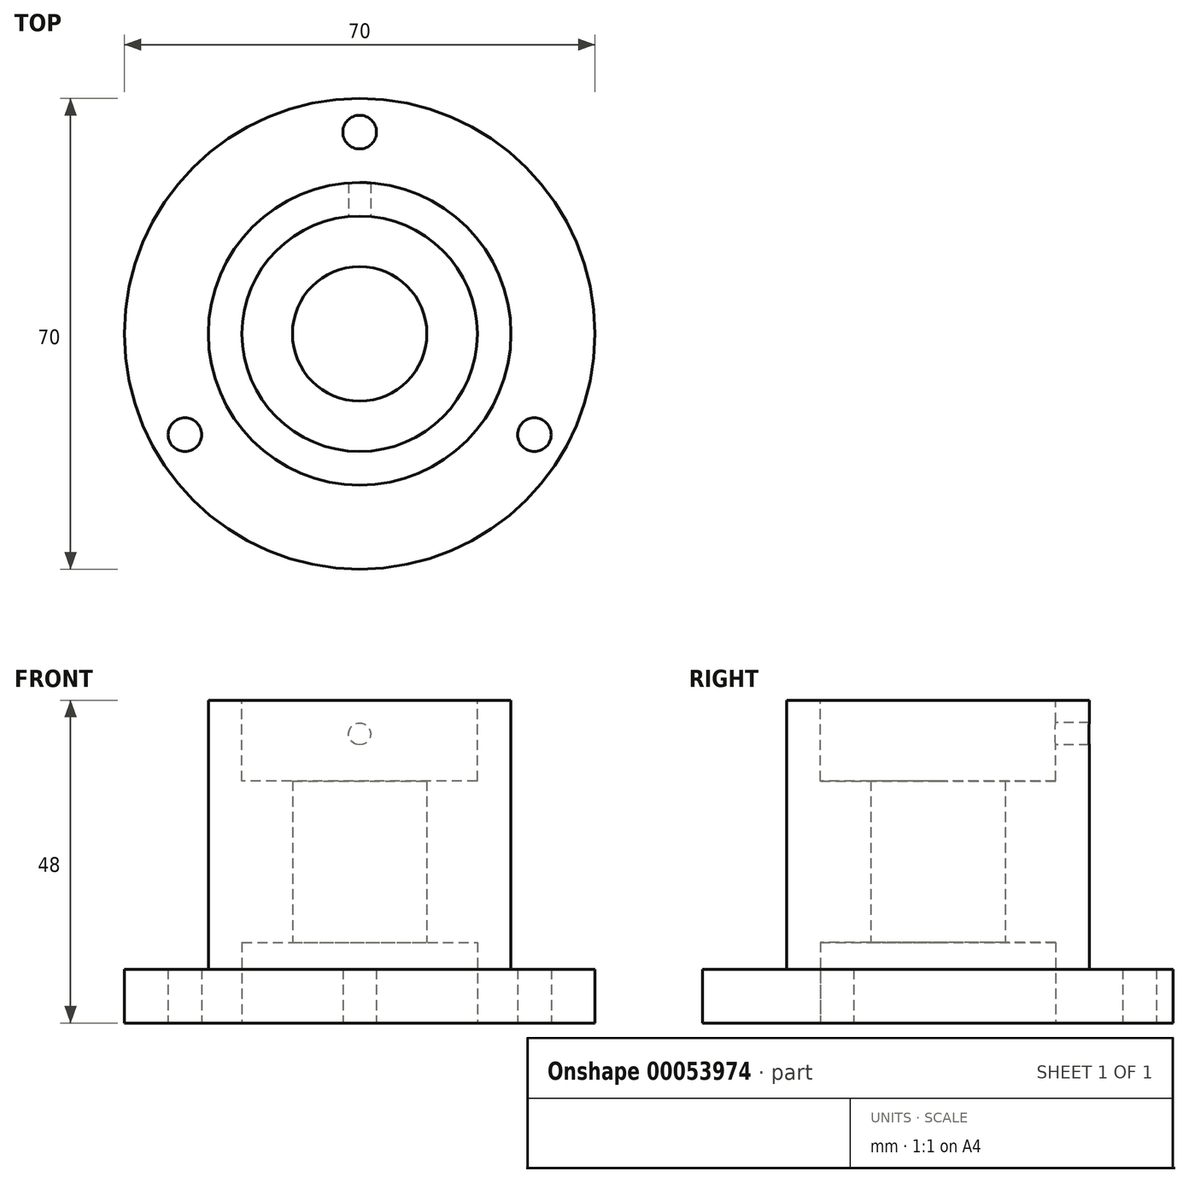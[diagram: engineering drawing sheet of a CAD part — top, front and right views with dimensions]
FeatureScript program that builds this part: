
annotation { "Feature Type Name" : "Feature", "Feature Type Description" : "" }
export const myFeature = defineFeature(function(context is Context, id is Id, definition is map)
    precondition{}
    {
        {
            var Q0;
            Q0=qCreatedBy(makeId("Top.planeOp"),FACE);
            var sketch = newSketch(context, id + "F0", { "sketchPlane" : qUnion([Q0])});
            skCircle(sketch, "E0", {"center": v(0, 0) * mm, "radius": 35 * mm});
            skSolve(sketch);
        }
        {
            var Q0;
            Q0 = qSketchRegion(id + "F0", true);
            extrude(context, id + "F1", {"entities" : qUnion([Q0]), "depth" : 8 * mm, "offsetDistance" : 25 * mm});
        }
        {
            var Q0;
            Q0=makeQuery(id+"F1.opExtrude","CAP_FACE",FACE,{"disambiguationData":[OSD([sQuery(id+"F0.wireOp",EDGE,"E0")])],"isStart":false});
            var sketch = newSketch(context, id + "F2", { "sketchPlane" : qUnion([Q0])});
            skCircle(sketch, "E1", {"center": v(0, 0) * mm, "radius": 22.5 * mm});
            skSolve(sketch);
        }
        {
            var Q0;
            Q0=makeQuery(id+"F2.imprint","IMPRINT",FACE,{"disambiguationData":[TD([[makeQuery(id+"F2.imprint","IMPRINT",EDGE,{"derivedFrom":sQuery(id+"F2.wireOp",EDGE,"E1")}),1.0]])]});
            extrude(context, id + "F3", {"entities" : qUnion([Q0]), "operationType" : NewBodyOperationType.ADD, "depth" : 40 * mm, "offsetDistance" : 25 * mm});
        }
        {
            var Q0;
            Q0=makeQuery(id+"F3.opExtrude","CAP_FACE",FACE,{"disambiguationData":[OSD([sQuery(id+"F2.wireOp",EDGE,"E1")])],"isStart":false});
            var sketch = newSketch(context, id + "F4", { "sketchPlane" : qUnion([Q0])});
            skCircle(sketch, "E2", {"center": v(0, 0) * mm, "radius": 17.5 * mm});
            skSolve(sketch);
        }
        {
            var Q0;
            Q0 = qSketchRegion(id + "F4", true);
            extrude(context, id + "F5", {"entities" : qUnion([Q0]), "operationType" : NewBodyOperationType.REMOVE, "oppositeDirection" : true, "depth" : 12 * mm, "offsetDistance" : 25 * mm});
        }
        {
            var Q0;
            Q0=makeQuery(id+"F1.opExtrude","CAP_FACE",FACE,{"disambiguationData":[OSD([sQuery(id+"F0.wireOp",EDGE,"E0")])],"isStart":true});
            var sketch = newSketch(context, id + "F6", { "sketchPlane" : qUnion([Q0])});
            skCircle(sketch, "E3", {"center": v(0, 0) * mm, "radius": 10 * mm});
            skSolve(sketch);
        }
        {
            var Q0;
            Q0 = qSketchRegion(id + "F6", true);
            extrude(context, id + "F7", {"entities" : qUnion([Q0]), "operationType" : NewBodyOperationType.REMOVE, "oppositeDirection" : true, "depth" : 50 * mm, "offsetDistance" : 25 * mm});
        }
        {
            var Q0;
            Q0=makeQuery(id+"F1.opExtrude","CAP_FACE",FACE,{"disambiguationData":[OSD([sQuery(id+"F0.wireOp",EDGE,"E0")])],"isStart":true});
            var sketch = newSketch(context, id + "F8", { "sketchPlane" : qUnion([Q0])});
            skPoint(sketch, "E4", {"position": v(0, -30) * mm});
            skPoint(sketch, "E5.1.0", {"position": v(25.98, 15) * mm});
            skPoint(sketch, "E5.2.0", {"position": v(-25.98, 15) * mm});
            skPoint(sketch, "E5.center", {"position": v(0, 0) * mm});
            skSolve(sketch);
        }
        {
            var Q0;
            Q0=sQuery(id+"F8.wireOp",VERTEX,"E4");
            var Q1;
            Q1=sQuery(id+"F8.wireOp",VERTEX,"E5.2.0");
            var Q2;
            Q2=sQuery(id+"F8.wireOp",VERTEX,"E5.1.0");
            var Q3;
            Q3=makeQuery(id+"F1.opExtrude","SWEPT_BODY",BODY,{"disambiguationData":[OSD([sQuery(id+"F0.wireOp",EDGE,"E0")])]});
            hole(context, id + "F9", {"style" : HoleStyle.SIMPLE, "endStyle" : HoleEndStyle.BLIND, "standardTappedOrClearance" : lookupTablePath({ "standard" : "ISO", "engagement" : "75%", "pitch" : "1 mm", "size" : "M6", "type" : "Tapped" }), "standardBlindInLast" : lookupTablePath({ "standard" : "ISO", "engagement" : "75%", "pitch" : "1 mm", "size" : "M6", "type" : "Tapped" }), "holeDiameter" : 5 * mm, "majorDiameter" : 6 * mm, "showTappedDepth" : true, "holeDepth" : 12 * mm, "isTappedThrough" : true, "tappedDepth" : 9 * mm, "tapClearance" : 3, "locations" : qUnion([Q0, Q1, Q2]), "scope" : qUnion([Q3])});
        }
        {
            var Q0;
            Q0=makeQuery(id+"F1.opExtrude","CAP_FACE",FACE,{"disambiguationData":[OSD([sQuery(id+"F0.wireOp",EDGE,"E0")])],"isStart":true});
            var sketch = newSketch(context, id + "F10", { "sketchPlane" : qUnion([Q0])});
            skCircle(sketch, "E6", {"center": v(0, 0) * mm, "radius": 17.5 * mm});
            skSolve(sketch);
        }
        {
            var Q0;
            Q0 = qSketchRegion(id + "F10", true);
            extrude(context, id + "F11", {"entities" : qUnion([Q0]), "operationType" : NewBodyOperationType.REMOVE, "oppositeDirection" : true, "depth" : 12 * mm, "offsetDistance" : 25 * mm});
        }
        {
            var Q0;
            Q0=qCreatedBy(makeId("Front.planeOp"),FACE);
            var sketch = newSketch(context, id + "F12", { "sketchPlane" : qUnion([Q0])});
            skPoint(sketch, "E7", {"position": v(0, 43) * mm});
            skSolve(sketch);
        }
        {
            var Q0;
            Q0=sQuery(id+"F12.wireOp",VERTEX,"E7");
            var Q1;
            Q1=makeQuery(id+"F1.opExtrude","SWEPT_BODY",BODY,{"disambiguationData":[OSD([sQuery(id+"F0.wireOp",EDGE,"E0")])]});
            hole(context, id + "F13", {"style" : HoleStyle.SIMPLE, "endStyle" : HoleEndStyle.BLIND, "standardTappedOrClearance" : lookupTablePath({ "standard" : "ISO", "engagement" : "75%", "pitch" : "0.7 mm", "size" : "M4", "type" : "Tapped" }), "standardBlindInLast" : lookupTablePath({ "standard" : "ISO", "engagement" : "75%", "pitch" : "0.7 mm", "size" : "M4", "type" : "Tapped" }), "holeDiameter" : 3.3 * mm, "majorDiameter" : 4 * mm, "showTappedDepth" : true, "holeDepth" : 11.1 * mm, "isTappedThrough" : true, "tappedDepth" : 9 * mm, "tapClearance" : 3, "locations" : qUnion([Q0]), "scope" : qUnion([Q1])});
        }
    });
